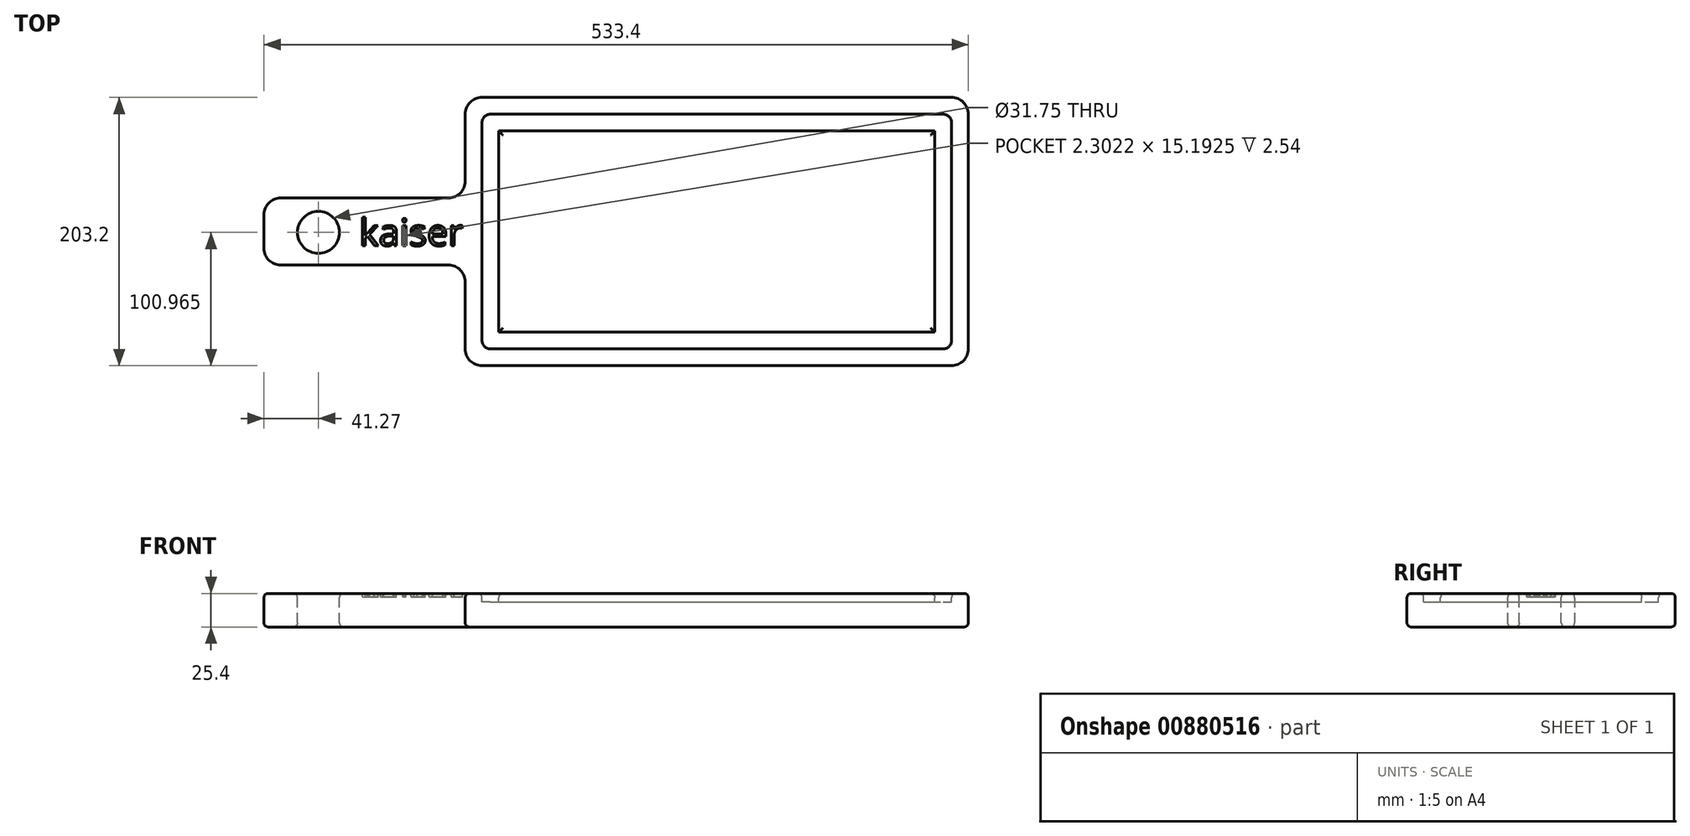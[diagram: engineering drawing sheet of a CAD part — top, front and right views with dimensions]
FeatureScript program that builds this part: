
annotation { "Feature Type Name" : "Feature", "Feature Type Description" : "" }
export const myFeature = defineFeature(function(context is Context, id is Id, definition is map)
    precondition{}
    {
        {
            var Q0;
            Q0=qCreatedBy(makeId("Top.planeOp"),FACE);
            var sketch = newSketch(context, id + "F0", { "sketchPlane" : qUnion([Q0])});
            skLineSegment(sketch, "E0.bottom", {"start": v(0, 0) * mm, "end": v(381, 0) * mm});
            skLineSegment(sketch, "E0.top", {"start": v(0, 203.2) * mm, "end": v(381, 203.2) * mm});
            skLineSegment(sketch, "E0.left", {"start": v(0, 0) * mm, "end": v(0, 203.2) * mm});
            skLineSegment(sketch, "E0.right", {"start": v(381, 0) * mm, "end": v(381, 203.2) * mm});
            skLineSegment(sketch, "E1.bottom", {"start": v(-152.4, 127) * mm, "end": v(0, 127) * mm});
            skLineSegment(sketch, "E1.top", {"start": v(-152.4, 76.2) * mm, "end": v(0, 76.2) * mm});
            skLineSegment(sketch, "E1.left", {"start": v(-152.4, 127) * mm, "end": v(-152.4, 76.2) * mm});
            skLineSegment(sketch, "E1.right", {"start": v(0, 127) * mm, "end": v(0, 76.2) * mm});
            skSolve(sketch);
        }
        {
            var Q0;
            {var subQ3=sQuery(id+"F0.wireOp",EDGE,"E0.bottom");Q0=makeQuery(id+"F0.imprint","IMPRINT",FACE,{"disambiguationData":[TD([[makeQuery(id+"F0.imprint","IMPRINT",EDGE,{"derivedFrom":subQ3}),1.0]])]});}
            var Q1;
            Q1=makeQuery(id+"F0.imprint","IMPRINT",FACE,{"disambiguationData":[TD([[makeQuery(id+"F0.imprint","IMPRINT",EDGE,{"derivedFrom":sQuery(id+"F0.wireOp",EDGE,"E1.bottom")}),-1.0]])]});
            extrude(context, id + "F1", {"entities" : qUnion([Q0, Q1]), "depth" : 25.4 * mm, "offsetDistance" : 25.4 * mm});
        }
        {
            var Q0;
            Q0=makeQuery(id+"F1.opExtrude","CAP_FACE",FACE,{"disambiguationData":[OSD([sQuery(id+"F0.wireOp",EDGE,"E0.bottom"),sQuery(id+"F0.wireOp",EDGE,"E0.top"),sQuery(id+"F0.wireOp",EDGE,"E0.left"),sQuery(id+"F0.wireOp",EDGE,"E0.right"),sQuery(id+"F0.wireOp",EDGE,"E1.bottom"),sQuery(id+"F0.wireOp",EDGE,"E1.top"),sQuery(id+"F0.wireOp",EDGE,"E1.left")])],"isStart":false});
            var sketch = newSketch(context, id + "F2", { "sketchPlane" : qUnion([Q0])});
            skCircle(sketch, "E2", {"center": v(-111.13, 100.97) * mm, "radius": 15.88 * mm});
            skSolve(sketch);
        }
        {
            var Q0;
            Q0 = qSketchRegion(id + "F2", true);
            extrude(context, id + "F3", {"entities" : qUnion([Q0]), "operationType" : NewBodyOperationType.REMOVE, "oppositeDirection" : true, "depth" : 25.4 * mm, "offsetDistance" : 25.4 * mm});
        }
        {
            var Q0;
            Q0=makeQuery(id+"F1.opExtrude","CAP_FACE",FACE,{"disambiguationData":[OSD([sQuery(id+"F0.wireOp",EDGE,"E0.bottom"),sQuery(id+"F0.wireOp",EDGE,"E0.top"),sQuery(id+"F0.wireOp",EDGE,"E0.left"),sQuery(id+"F0.wireOp",EDGE,"E0.right"),sQuery(id+"F0.wireOp",EDGE,"E1.bottom"),sQuery(id+"F0.wireOp",EDGE,"E1.top"),sQuery(id+"F0.wireOp",EDGE,"E1.left")])],"isStart":false});
            var sketch = newSketch(context, id + "F4", { "sketchPlane" : qUnion([Q0])});
            skLineSegment(sketch, "E3", {"start": v(0, 127) * mm, "end": v(0, 76.2) * mm});
            skLineSegment(sketch, "E4.0", {"start": v(12.7, 127) * mm, "end": v(12.7, 190.5) * mm});
            skLineSegment(sketch, "E4.1", {"start": v(368.3, 12.7) * mm, "end": v(368.3, 190.5) * mm});
            skLineSegment(sketch, "E4.2", {"start": v(12.7, 12.7) * mm, "end": v(368.3, 12.7) * mm});
            skLineSegment(sketch, "E4.3", {"start": v(12.7, 190.5) * mm, "end": v(368.3, 190.5) * mm});
            skLineSegment(sketch, "E4.4", {"start": v(12.7, 12.7) * mm, "end": v(12.7, 76.2) * mm});
            skLineSegment(sketch, "E4.5", {"start": v(12.7, 127) * mm, "end": v(12.7, 76.2) * mm});
            skLineSegment(sketch, "E5.0", {"start": v(25.4, 127) * mm, "end": v(25.4, 177.8) * mm});
            skLineSegment(sketch, "E5.1", {"start": v(355.6, 25.4) * mm, "end": v(355.6, 177.8) * mm});
            skLineSegment(sketch, "E5.2", {"start": v(25.4, 25.4) * mm, "end": v(355.6, 25.4) * mm});
            skLineSegment(sketch, "E5.3", {"start": v(25.4, 177.8) * mm, "end": v(355.6, 177.8) * mm});
            skLineSegment(sketch, "E5.4", {"start": v(25.4, 25.4) * mm, "end": v(25.4, 76.2) * mm});
            skLineSegment(sketch, "E5.5", {"start": v(25.4, 127) * mm, "end": v(25.4, 76.2) * mm});
            skSolve(sketch);
        }
        {
            var Q0;
            Q0=makeQuery(id+"F4.imprint","IMPRINT",FACE,{"disambiguationData":[TD([[makeQuery(id+"F4.imprint","IMPRINT",EDGE,{"derivedFrom":sQuery(id+"F4.wireOp",EDGE,"E4.0")}),-1.0]])]});
            extrude(context, id + "F5", {"entities" : qUnion([Q0]), "operationType" : NewBodyOperationType.REMOVE, "oppositeDirection" : true, "depth" : 6.35 * mm, "offsetDistance" : 25.4 * mm});
        }
        {
            var Q0;
            Q0=makeQuery(id+"F5.boolean.opBoolean","COPY",EDGE,{"derivedFrom":makeQuery(id+"F5.opExtrude","SWEPT_EDGE",EDGE,{"disambiguationData":[OSD([sQuery(id+"F4.wireOp",EDGE,"E4.0"),sQuery(id+"F4.wireOp",EDGE,"E4.3")])]})});
            var Q1;
            Q1=makeQuery(id+"F5.boolean.opBoolean","COPY",EDGE,{"derivedFrom":makeQuery(id+"F5.opExtrude","SWEPT_EDGE",EDGE,{"disambiguationData":[OSD([sQuery(id+"F4.wireOp",EDGE,"E4.1"),sQuery(id+"F4.wireOp",EDGE,"E4.3")])]})});
            var Q2;
            Q2=makeQuery(id+"F5.boolean.opBoolean","COPY",EDGE,{"derivedFrom":makeQuery(id+"F5.opExtrude","SWEPT_EDGE",EDGE,{"disambiguationData":[OSD([sQuery(id+"F4.wireOp",EDGE,"E4.2"),sQuery(id+"F4.wireOp",EDGE,"E4.4")])]})});
            var Q3;
            Q3=makeQuery(id+"F5.boolean.opBoolean","COPY",EDGE,{"derivedFrom":makeQuery(id+"F5.opExtrude","SWEPT_EDGE",EDGE,{"disambiguationData":[OSD([sQuery(id+"F4.wireOp",EDGE,"E4.1"),sQuery(id+"F4.wireOp",EDGE,"E4.2")])]})});
            fillet(context, id + "F6", {"entities" : qUnion([Q0, Q1, Q2, Q3]), "radius" : 6.35 * mm, "tangentPropagation" : true, "allowEdgeOverflow" : false});
        }
        {
            var Q0;
            Q0=makeQuery(id+"F1.opExtrude","SWEPT_EDGE",EDGE,{"disambiguationData":[OSD([sQuery(id+"F0.wireOp",EDGE,"E0.top"),sQuery(id+"F0.wireOp",EDGE,"E0.right")])]});
            var Q1;
            Q1=makeQuery(id+"F1.opExtrude","SWEPT_EDGE",EDGE,{"disambiguationData":[OSD([sQuery(id+"F0.wireOp",EDGE,"E0.top"),sQuery(id+"F0.wireOp",EDGE,"E0.left")])]});
            var Q2;
            Q2=makeQuery(id+"F1.opExtrude","SWEPT_EDGE",EDGE,{"disambiguationData":[OSD([sQuery(id+"F0.wireOp",EDGE,"E0.bottom"),sQuery(id+"F0.wireOp",EDGE,"E0.left")])]});
            var Q3;
            Q3=makeQuery(id+"F1.opExtrude","SWEPT_EDGE",EDGE,{"disambiguationData":[OSD([sQuery(id+"F0.wireOp",EDGE,"E0.bottom"),sQuery(id+"F0.wireOp",EDGE,"E0.right")])]});
            fillet(context, id + "F7", {"entities" : qUnion([Q0, Q1, Q2, Q3]), "radius" : 12.7 * mm, "tangentPropagation" : true, "allowEdgeOverflow" : false});
        }
        {
            var Q0;
            Q0=makeQuery(id+"F1.opExtrude","SWEPT_EDGE",EDGE,{"disambiguationData":[OSD([sQuery(id+"F0.wireOp",EDGE,"E0.left"),sQuery(id+"F0.wireOp",EDGE,"E1.bottom"),sQuery(id+"F0.wireOp",EDGE,"E1.right")])]});
            var Q1;
            Q1=makeQuery(id+"F1.opExtrude","SWEPT_EDGE",EDGE,{"disambiguationData":[OSD([sQuery(id+"F0.wireOp",EDGE,"E1.bottom"),sQuery(id+"F0.wireOp",EDGE,"E1.left")])]});
            var Q2;
            Q2=makeQuery(id+"F1.opExtrude","SWEPT_EDGE",EDGE,{"disambiguationData":[OSD([sQuery(id+"F0.wireOp",EDGE,"E1.top"),sQuery(id+"F0.wireOp",EDGE,"E1.left")])]});
            var Q3;
            Q3=makeQuery(id+"F1.opExtrude","SWEPT_EDGE",EDGE,{"disambiguationData":[OSD([sQuery(id+"F0.wireOp",EDGE,"E0.left"),sQuery(id+"F0.wireOp",EDGE,"E1.top"),sQuery(id+"F0.wireOp",EDGE,"E1.right")])]});
            fillet(context, id + "F8", {"entities" : qUnion([Q0, Q1, Q2, Q3]), "radius" : 12.7 * mm, "tangentPropagation" : true, "allowEdgeOverflow" : false});
        }
        {
            var Q0;
            Q0=makeQuery(id+"F5.boolean.opBoolean","SPLIT",FACE,{"disambiguationData":[TD([makeQuery(id+"F5.opExtrude","SWEPT_FACE",FACE,{"disambiguationData":[OSD([sQuery(id+"F4.wireOp",EDGE,"E5.1")])]})])],"derivedFrom":makeQuery(id+"F1.opExtrude","CAP_FACE",FACE,{"disambiguationData":[OSD([sQuery(id+"F0.wireOp",EDGE,"E0.bottom"),sQuery(id+"F0.wireOp",EDGE,"E0.top"),sQuery(id+"F0.wireOp",EDGE,"E0.left"),sQuery(id+"F0.wireOp",EDGE,"E0.right"),sQuery(id+"F0.wireOp",EDGE,"E1.bottom"),sQuery(id+"F0.wireOp",EDGE,"E1.top"),sQuery(id+"F0.wireOp",EDGE,"E1.left")])],"isStart":false})});
            var Q1;
            {var subQ0=sQuery(id+"F0.wireOp",EDGE,"E0.left");var subQ1=sQuery(id+"F0.wireOp",EDGE,"E0.top");var subQ3=sQuery(id+"F0.wireOp",EDGE,"E1.bottom");var subQ4=sQuery(id+"F0.wireOp",EDGE,"E1.left");var subQ5=sQuery(id+"F0.wireOp",EDGE,"E1.top");var subQ6=sQuery(id+"F0.wireOp",EDGE,"E0.right");var subQ7=sQuery(id+"F0.wireOp",EDGE,"E0.bottom");Q1=makeQuery(id+"F5.boolean.opBoolean","SPLIT",FACE,{"disambiguationData":[TD([makeQuery(id+"F1.opExtrude","SWEPT_FACE",FACE,{"disambiguationData":[OSD([subQ7])]})])],"derivedFrom":makeQuery(id+"F1.opExtrude","CAP_FACE",FACE,{"disambiguationData":[OSD([subQ7,subQ1,subQ0,subQ6,subQ3,subQ5,subQ4])],"isStart":false})});}
            var Q2;
            Q2=makeQuery(id+"F1.opExtrude","CAP_FACE",FACE,{"disambiguationData":[OSD([sQuery(id+"F0.wireOp",EDGE,"E0.bottom"),sQuery(id+"F0.wireOp",EDGE,"E0.top"),sQuery(id+"F0.wireOp",EDGE,"E0.left"),sQuery(id+"F0.wireOp",EDGE,"E0.right"),sQuery(id+"F0.wireOp",EDGE,"E1.bottom"),sQuery(id+"F0.wireOp",EDGE,"E1.top"),sQuery(id+"F0.wireOp",EDGE,"E1.left")])],"isStart":true});
            fillet(context, id + "F9", {"entities" : qUnion([Q0, Q1, Q2]), "radius" : 3.17 * mm, "tangentPropagation" : true, "allowEdgeOverflow" : false});
        }
        {
            var Q0;
            {var subQ0=sQuery(id+"F0.wireOp",EDGE,"E0.left");var subQ1=sQuery(id+"F0.wireOp",EDGE,"E0.top");var subQ3=sQuery(id+"F0.wireOp",EDGE,"E1.bottom");var subQ4=sQuery(id+"F0.wireOp",EDGE,"E1.left");var subQ5=sQuery(id+"F0.wireOp",EDGE,"E1.top");var subQ6=sQuery(id+"F0.wireOp",EDGE,"E0.right");var subQ7=sQuery(id+"F0.wireOp",EDGE,"E0.bottom");Q0=makeQuery(id+"F5.boolean.opBoolean","SPLIT",FACE,{"disambiguationData":[TD([makeQuery(id+"F1.opExtrude","SWEPT_FACE",FACE,{"disambiguationData":[OSD([subQ7])]})])],"derivedFrom":makeQuery(id+"F1.opExtrude","CAP_FACE",FACE,{"disambiguationData":[OSD([subQ7,subQ1,subQ0,subQ6,subQ3,subQ5,subQ4])],"isStart":false})});}
            var sketch = newSketch(context, id + "F10", { "sketchPlane" : qUnion([Q0])});
            skText(sketch, "E6", { "text": "  kaiser", "fontName": "OpenSans-Regular.ttf"});
            const initialGuessF10  = {"E6": [-0.09511, 0.09084, 1, 0, 0.02044]};
            skSetInitialGuess(sketch, initialGuessF10);
            skSolve(sketch);
        }
        {
            var Q0;
            Q0 = qSketchRegion(id + "F10", true);
            extrude(context, id + "F11", {"entities" : qUnion([Q0]), "operationType" : NewBodyOperationType.REMOVE, "oppositeDirection" : true, "depth" : 2.54 * mm, "offsetDistance" : 25.4 * mm});
        }
    });
